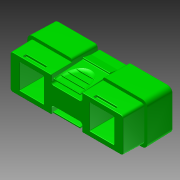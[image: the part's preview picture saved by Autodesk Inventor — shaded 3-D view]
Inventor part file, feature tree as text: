
AUTODESK INVENTOR PART (.ipt)
format: ipt  version: 2015 (Build 190159000, 159)  size: 1,799,168 bytes
history: native  units: in
note: dims shown in document units (in); Inventor stores cm internally (conversion verified against a paired STEP export)
features: extrude x8, fillet x8, sketch x7, draft x4, mirror x2, projected_geometry x1
ambient origin geometry x8: Origin, YZ Plane, XZ Plane, XY Plane, X Axis, Y Axis, Z Axis, Center Point
bodies: Solid1 (feature_tree)
feature tree (30):
  sketch  "Sketch1"  dims[d0=0.34in d1=0.8in]
  extrude  "Extrusion1"  Depth=0.8in
  extrude  "Extrusion2"  Depth=0.2975in
  extrude  "Extrusion3"  Depth=0.06in
  draft  "FaceDraft1"
  draft  "FaceDraft2"
  extrude  "Extrusion4"  Depth=0.5in TaperAngle=0.0deg
  extrude  "Extrusion5"  Depth=0.15in
  fillet  "Fillet1"  Radius=0.33in
  fillet  "Fillet2"  Radius=0.0069in
  extrude  "Extrusion6"  Depth=0.17in
  draft  "FaceDraft3"
  fillet  "Fillet3"  Radius=0.17in
  fillet  "Fillet4"  Radius=0.04in
  fillet  "Fillet5"  Radius=0.09in
  extrude  "Extrusion7"  Depth=0.03in
  extrude  "Extrusion8"  Depth=0.33in
  draft  "FaceDraft4"
  fillet  "Fillet6"  Radius=0.0206in
  fillet  "Fillet7"  Radius=0.0412in
  fillet  "Fillet8"  Radius=0.2625in
  mirror  "Mirror1"
  mirror  "Mirror2"
  sketch  "Sketch2"  dims[d2=0.175in d3=0.2975in]
  sketch  "Sketch3"  dims[d4=0.06in d5=0.06in]
  sketch  "Sketch4"  dims[d6=0.4in d7=0.0in d8=0.5in d9=0.0in]
  projected_geometry  "Projected Loop1"
  sketch  "Sketch5"  dims[d11=0.8in d12=0.15in d13=0.33in d14=0.0in d15=0.0069in]
  sketch  "Sketch6"  dims[d16=0.0069in d17=0.17in d18=0.17in d19=0.04in d20=0.09in]
  sketch  "Sketch7"  dims[d21=0.84in d22=0.03in d24=0.33in d25=0.0206in d26=0.0412in d27=0.2625in d28=0.0in d31=0.25in d32=0.1in d33=0.2in d34=0.6174in d35=0.01in d36=0.02in d37=0.0in d38=0.05in d39=0.185in d40=0.02in d41=0.125in d42=0.24in d43=0.36in d44=0.26in d45=0.01in d46=0.01in d47=0.0in d48=0.0137in d49=0.4in d50=0.06in d51=0.48in d52=0.3in d53=0.04in d54=0.0in d55=0.2375in d56=0.47in d57=0.186in d58=0.47in d59=0.0in d60=0.0069in d61=0.05in d62=0.01in d63=0.005in d64=0.1in]
